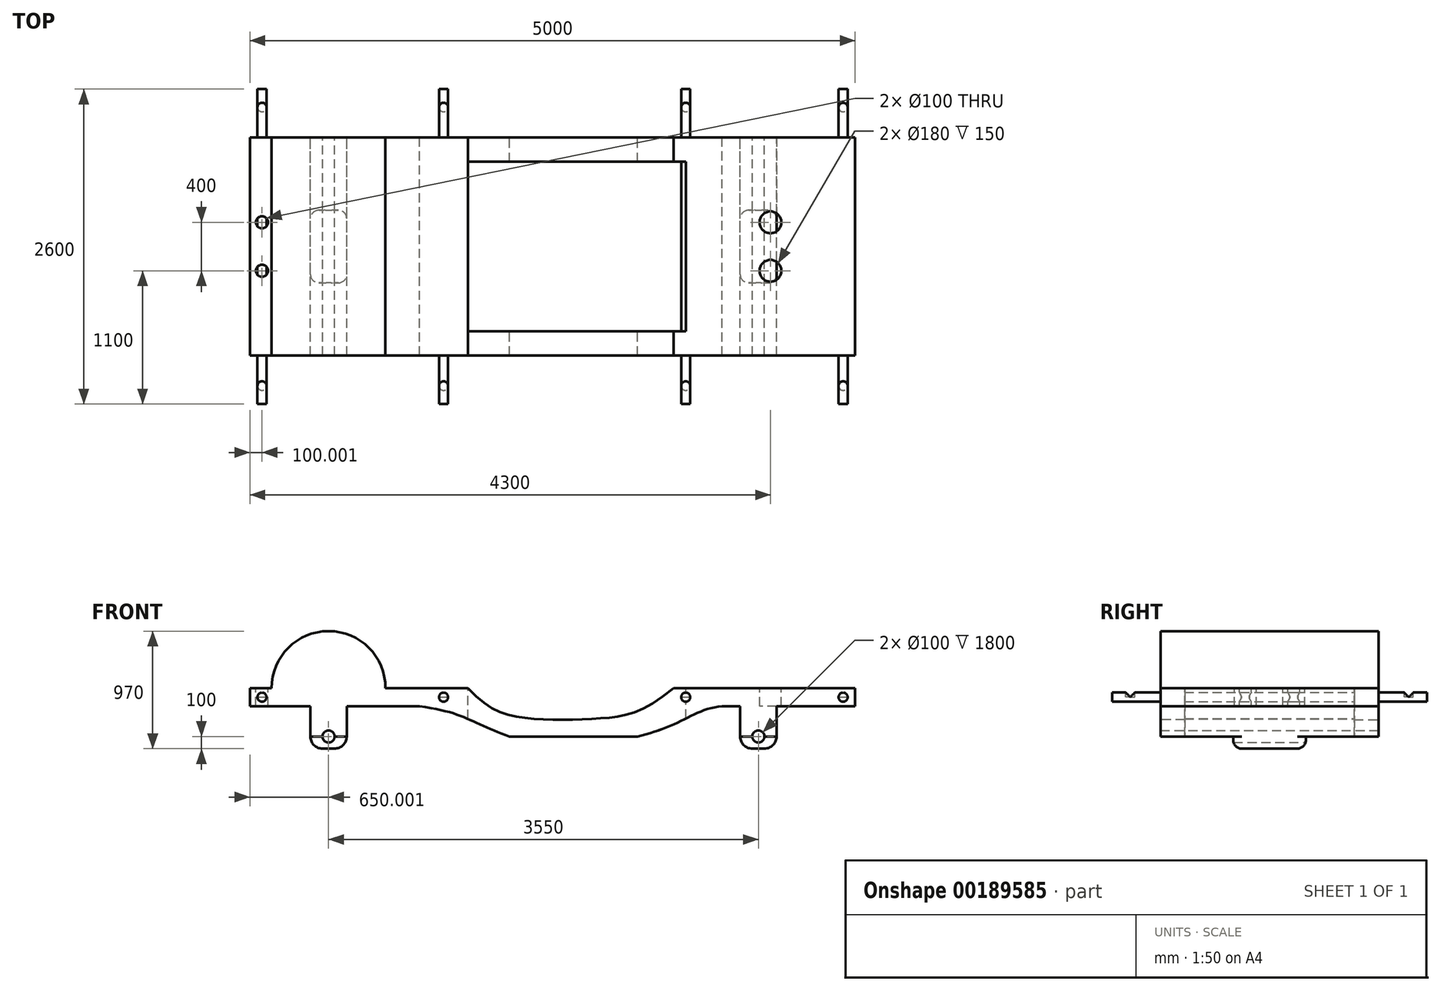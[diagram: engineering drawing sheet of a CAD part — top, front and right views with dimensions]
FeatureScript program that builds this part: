
annotation { "Feature Type Name" : "Feature", "Feature Type Description" : "" }
export const myFeature = defineFeature(function(context is Context, id is Id, definition is map)
    precondition{}
    {
        {
            var Q0;
            Q0=qCreatedBy(makeId("Front.planeOp"),FACE);
            var sketch = newSketch(context, id + "F0", { "sketchPlane" : qUnion([Q0])});
            skLineSegment(sketch, "E0", {"start": v(-2207.1, 0) * mm, "end": v(-2207.1, -150) * mm});
            skLineSegment(sketch, "E1", {"start": v(-2207.1, -150) * mm, "end": v(-807.1, -150) * mm});
            skFitSpline(sketch, "E2", {"points": [v(-807.1, -150) * mm, v(-307.1, -300) * mm, v(192.9, -450) * mm], "startDerivative": vector(1549.63, -206.62) * mm, "endDerivative": vector(1157.34, -66.43) * mm});
            skFitSpline(sketch, "E3", {"points": [v(192.9, -450) * mm, v(692.9, -450) * mm, v(1292.9, -300) * mm, v(1692.9, -150) * mm], "startDerivative": vector(931.79, -77.59) * mm, "endDerivative": vector(1482.21, 107.32) * mm});
            skLineSegment(sketch, "E4", {"start": v(1692.9, -150) * mm, "end": v(2792.9, -150) * mm});
            skLineSegment(sketch, "E5", {"start": v(2792.9, -150) * mm, "end": v(2792.9, 0) * mm});
            skLineSegment(sketch, "E6", {"start": v(-2207.1, 0) * mm, "end": v(-407.1, 0) * mm});
            skFitSpline(sketch, "E7", {"points": [v(-407.1, 0) * mm, v(92.9, -250) * mm, v(693, -250) * mm, v(1293, 0) * mm], "startDerivative": vector(1561.36, -1754.44) * mm, "endDerivative": vector(2212.71, 1856.89) * mm});
            skLineSegment(sketch, "E8", {"start": v(1293, 0) * mm, "end": v(2792.9, 0) * mm});
            skSolve(sketch);
        }
        {
            var Q0;
            Q0 = qSketchRegion(id + "F0", true);
            extrude(context, id + "F1", {"entities" : qUnion([Q0]), "depth" : 1800 * mm});
        }
        {
            var Q0;
            Q0=qCreatedBy(makeId("Top.planeOp"),FACE);
            var sketch = newSketch(context, id + "F2", { "sketchPlane" : qUnion([Q0])});
            skLineSegment(sketch, "E9.bottom", {"start": v(-407.1, -200) * mm, "end": v(1392.9, -200) * mm});
            skLineSegment(sketch, "E9.top", {"start": v(-407.1, -1600) * mm, "end": v(1392.9, -1600) * mm});
            skLineSegment(sketch, "E9.left", {"start": v(-407.1, -200) * mm, "end": v(-407.1, -1600) * mm});
            skLineSegment(sketch, "E9.right", {"start": v(1392.9, -200) * mm, "end": v(1392.9, -1600) * mm});
            skCircle(sketch, "E10", {"center": v(2092.9, -700) * mm, "radius": 90 * mm});
            skCircle(sketch, "E11", {"center": v(2092.9, -1100) * mm, "radius": 90 * mm});
            skCircle(sketch, "E12", {"center": v(-2107.1, -700) * mm, "radius": 50 * mm});
            skCircle(sketch, "E13", {"center": v(-2107.1, -1100) * mm, "radius": 50 * mm});
            skLineSegment(sketch, "E14", {"start": v(-2433.44, -900) * mm, "end": v(3216.39, -900) * mm, "construction": true});
            skSolve(sketch);
        }
        {
            var Q0;
            Q0=makeQuery(id+"F2.imprint","IMPRINT",FACE,{"disambiguationData":[TD([[makeQuery(id+"F2.imprint","IMPRINT",EDGE,{"derivedFrom":sQuery(id+"F2.wireOp",EDGE,"2RptNs6A-mePP-rphL-eACh-eVUUGwHWJbpe.bottom")}),-1.0]])]});
            var Q1;
            Q1=makeQuery(id+"F2.imprint","IMPRINT",FACE,{"disambiguationData":[TD([[makeQuery(id+"F2.imprint","IMPRINT",EDGE,{"derivedFrom":sQuery(id+"F2.wireOp",EDGE,"E9.bottom")}),-1.0]])]});
            var Q2;
            Q2=makeQuery(id+"F2.imprint","IMPRINT",FACE,{"disambiguationData":[TD([[makeQuery(id+"F2.imprint","IMPRINT",EDGE,{"derivedFrom":sQuery(id+"F2.wireOp",EDGE,"kMBfGQrs-vHd1-vmnO-5CYD-BuNOrFmh5Xz2.bottom")}),1.0]])]});
            var Q3;
            Q3=makeQuery(id+"F2.imprint","IMPRINT",FACE,{"disambiguationData":[TD([[makeQuery(id+"F2.imprint","IMPRINT",EDGE,{"derivedFrom":sQuery(id+"F2.wireOp",EDGE,"E11")}),1.0]])]});
            var Q4;
            Q4=makeQuery(id+"F2.imprint","IMPRINT",FACE,{"disambiguationData":[TD([[makeQuery(id+"F2.imprint","IMPRINT",EDGE,{"derivedFrom":sQuery(id+"F2.wireOp",EDGE,"E10")}),1.0]])]});
            var Q5;
            Q5=makeQuery(id+"F2.imprint","IMPRINT",FACE,{"disambiguationData":[TD([[makeQuery(id+"F2.imprint","IMPRINT",EDGE,{"derivedFrom":sQuery(id+"F2.wireOp",EDGE,"E12")}),1.0]])]});
            var Q6;
            Q6=makeQuery(id+"F2.imprint","IMPRINT",FACE,{"disambiguationData":[TD([[makeQuery(id+"F2.imprint","IMPRINT",EDGE,{"derivedFrom":sQuery(id+"F2.wireOp",EDGE,"E13")}),1.0]])]});
            extrude(context, id + "F3", {"entities" : qUnion([Q0, Q1, Q2, Q3, Q4, Q5, Q6]), "operationType" : NewBodyOperationType.REMOVE, "oppositeDirection" : true, "depth" : 1000 * mm, "hasSecondDirection" : true, "secondDirectionOppositeDirection" : false, "secondDirectionDepth" : 680 * mm});
        }
        {
            var Q0;
            Q0=makeQuery(id+"F2.imprint","IMPRINT",FACE,{"disambiguationData":[TD([[makeQuery(id+"F2.imprint","IMPRINT",EDGE,{"derivedFrom":sQuery(id+"F2.wireOp",EDGE,"E9.bottom")}),-1.0]])]});
            extrude(context, id + "F4", {"entities" : qUnion([Q0]), "operationType" : NewBodyOperationType.REMOVE, "depth" : 25 * mm});
        }
        {
            var Q0;
            Q0=qCreatedBy(makeId("Front.planeOp"),FACE);
            var sketch = newSketch(context, id + "F5", { "sketchPlane" : qUnion([Q0])});
            skLineSegment(sketch, "E15.bottom", {"start": v(1842.9, -150) * mm, "end": v(2142.9, -150) * mm});
            skLineSegment(sketch, "E15.top", {"start": v(1842.9, -500) * mm, "end": v(2142.9, -500) * mm});
            skLineSegment(sketch, "E15.left", {"start": v(1842.9, -150) * mm, "end": v(1842.9, -500) * mm});
            skLineSegment(sketch, "E15.right", {"start": v(2142.9, -150) * mm, "end": v(2142.9, -500) * mm});
            skLineSegment(sketch, "E16.bottom", {"start": v(-1707.1, -150) * mm, "end": v(-1407.1, -150) * mm});
            skLineSegment(sketch, "E16.top", {"start": v(-1707.1, -500) * mm, "end": v(-1407.1, -500) * mm});
            skLineSegment(sketch, "E16.left", {"start": v(-1707.1, -150) * mm, "end": v(-1707.1, -500) * mm});
            skLineSegment(sketch, "E16.right", {"start": v(-1407.1, -150) * mm, "end": v(-1407.1, -500) * mm});
            skCircle(sketch, "E17", {"center": v(-1557.1, -400) * mm, "radius": 50 * mm});
            skCircle(sketch, "E18", {"center": v(1992.9, -400) * mm, "radius": 50 * mm});
            skSolve(sketch);
        }
        {
            var Q0;
            Q0=makeQuery(id+"F5.imprint","IMPRINT",FACE,{"disambiguationData":[TD([[makeQuery(id+"F5.imprint","IMPRINT",EDGE,{"derivedFrom":sQuery(id+"F5.wireOp",EDGE,"E15.bottom")}),-1.0]])]});
            var Q1;
            Q1=makeQuery(id+"F5.imprint","IMPRINT",FACE,{"disambiguationData":[TD([[makeQuery(id+"F5.imprint","IMPRINT",EDGE,{"derivedFrom":sQuery(id+"F5.wireOp",EDGE,"E16.bottom")}),-1.0]])]});
            extrude(context, id + "F6", {"entities" : qUnion([Q0, Q1]), "operationType" : NewBodyOperationType.ADD, "depth" : 1800 * mm});
        }
        {
            var Q0;
            Q0=makeQuery(id+"F6.opExtrude","SWEPT_EDGE",EDGE,{"disambiguationData":[OSD([sQuery(id+"F5.wireOp",EDGE,"E16.top"),sQuery(id+"F5.wireOp",EDGE,"E16.left")])]});
            var Q1;
            Q1=makeQuery(id+"F6.opExtrude","SWEPT_EDGE",EDGE,{"disambiguationData":[OSD([sQuery(id+"F5.wireOp",EDGE,"E16.top"),sQuery(id+"F5.wireOp",EDGE,"E16.right")])]});
            var Q2;
            Q2=makeQuery(id+"F6.opExtrude","SWEPT_EDGE",EDGE,{"disambiguationData":[OSD([sQuery(id+"F5.wireOp",EDGE,"E15.top"),sQuery(id+"F5.wireOp",EDGE,"E15.left")])]});
            var Q3;
            Q3=makeQuery(id+"F6.opExtrude","SWEPT_EDGE",EDGE,{"disambiguationData":[OSD([sQuery(id+"F5.wireOp",EDGE,"E15.top"),sQuery(id+"F5.wireOp",EDGE,"E15.right")])]});
            fillet(context, id + "F7", {"entities" : qUnion([Q0, Q1, Q2, Q3]), "radius" : 100 * mm, "tangentPropagation" : true, "allowEdgeOverflow" : false});
        }
        {
            var Q0;
            Q0=makeQuery(id+"F6.opExtrude","SWEPT_FACE",FACE,{"disambiguationData":[OSD([sQuery(id+"F5.wireOp",EDGE,"E16.left")])]});
            var sketch = newSketch(context, id + "F8", { "sketchPlane" : qUnion([Q0])});
            skLineSegment(sketch, "E19.bottom", {"start": v(0, -550) * mm, "end": v(600, -550) * mm});
            skLineSegment(sketch, "E19.top", {"start": v(0, -400) * mm, "end": v(600, -400) * mm});
            skLineSegment(sketch, "E19.left", {"start": v(0, -550) * mm, "end": v(0, -400) * mm});
            skLineSegment(sketch, "E19.right", {"start": v(600, -550) * mm, "end": v(600, -400) * mm});
            skLineSegment(sketch, "E20.bottom", {"start": v(1200, -550) * mm, "end": v(1800, -550) * mm});
            skLineSegment(sketch, "E20.top", {"start": v(1200, -400) * mm, "end": v(1800, -400) * mm});
            skLineSegment(sketch, "E20.left", {"start": v(1200, -550) * mm, "end": v(1200, -400) * mm});
            skLineSegment(sketch, "E20.right", {"start": v(1800, -550) * mm, "end": v(1800, -400) * mm});
            skSolve(sketch);
        }
        {
            var Q0;
            {var subQ0=sQuery(id+"F8.wireOp",EDGE,"E20.bottom");Q0=makeQuery(id+"F8.imprint","IMPRINT",FACE,{"disambiguationData":[TD([[makeQuery(id+"F8.imprint","IMPRINT",EDGE,{"derivedFrom":subQ0}),1.0]])]});}
            var Q1;
            {var subQ0=sQuery(id+"F8.wireOp",EDGE,"E20.top");Q1=makeQuery(id+"F8.imprint","IMPRINT",FACE,{"disambiguationData":[TD([[makeQuery(id+"F8.imprint","IMPRINT",EDGE,{"derivedFrom":subQ0}),-1.0]])]});}
            var Q2;
            {var subQ0=sQuery(id+"F8.wireOp",EDGE,"E19.top");Q2=makeQuery(id+"F8.imprint","IMPRINT",FACE,{"disambiguationData":[TD([[makeQuery(id+"F8.imprint","IMPRINT",EDGE,{"derivedFrom":subQ0}),-1.0]])]});}
            var Q3;
            {var subQ0=sQuery(id+"F8.wireOp",EDGE,"E19.bottom");Q3=makeQuery(id+"F8.imprint","IMPRINT",FACE,{"disambiguationData":[TD([[makeQuery(id+"F8.imprint","IMPRINT",EDGE,{"derivedFrom":subQ0}),1.0]])]});}
            extrude(context, id + "F9", {"entities" : qUnion([Q0, Q1, Q2, Q3]), "operationType" : NewBodyOperationType.REMOVE, "oppositeDirection" : true, "depth" : 4000 * mm});
        }
        {
            var Q0;
            {var subQ0=sQuery(id+"F5.wireOp",EDGE,"E15.top");var subQ1=sQuery(id+"F8.wireOp",EDGE,"E19.right");Q0=makeQuery(id+"F9.boolean.opBoolean","COPY",EDGE,{"disambiguationData":[TD([makeQuery(id+"F6.opExtrude","SWEPT_FACE",FACE,{"disambiguationData":[OSD([subQ0])]})])],"derivedFrom":makeQuery(id+"F9.opExtrude","SWEPT_EDGE",EDGE,{"disambiguationData":[OSD([sQuery(id+"F8.wireOp",EDGE,"E19.bottom"),subQ1])]})});}
            var Q1;
            Q1=makeQuery(id+"F9.boolean.opBoolean","INTERSECT",EDGE,{"derivedFrom":[makeQuery(id+"F7.opFillet","BLEND_FACE",FACE,{"disambiguationData":[OSD([sQuery(id+"F5.wireOp",EDGE,"E15.top"),sQuery(id+"F5.wireOp",EDGE,"E15.right")])]}),makeQuery(id+"F9.opExtrude","SWEPT_FACE",FACE,{"disambiguationData":[OSD([sQuery(id+"F8.wireOp",EDGE,"E19.right")])]})]});
            var Q2;
            Q2=makeQuery(id+"F9.boolean.opBoolean","INTERSECT",EDGE,{"derivedFrom":[makeQuery(id+"F7.opFillet","BLEND_FACE",FACE,{"disambiguationData":[OSD([sQuery(id+"F5.wireOp",EDGE,"E15.top"),sQuery(id+"F5.wireOp",EDGE,"E15.right")])]}),makeQuery(id+"F9.opExtrude","SWEPT_FACE",FACE,{"disambiguationData":[OSD([sQuery(id+"F8.wireOp",EDGE,"E20.left")])]})]});
            var Q3;
            Q3=makeQuery(id+"F9.boolean.opBoolean","INTERSECT",EDGE,{"derivedFrom":[makeQuery(id+"F7.opFillet","BLEND_FACE",FACE,{"disambiguationData":[OSD([sQuery(id+"F5.wireOp",EDGE,"E16.top"),sQuery(id+"F5.wireOp",EDGE,"E16.left")])]}),makeQuery(id+"F9.opExtrude","SWEPT_FACE",FACE,{"disambiguationData":[OSD([sQuery(id+"F8.wireOp",EDGE,"E19.right")])]})]});
            var Q4;
            Q4=makeQuery(id+"F9.boolean.opBoolean","INTERSECT",EDGE,{"derivedFrom":[makeQuery(id+"F7.opFillet","BLEND_FACE",FACE,{"disambiguationData":[OSD([sQuery(id+"F5.wireOp",EDGE,"E16.top"),sQuery(id+"F5.wireOp",EDGE,"E16.left")])]}),makeQuery(id+"F9.opExtrude","SWEPT_FACE",FACE,{"disambiguationData":[OSD([sQuery(id+"F8.wireOp",EDGE,"E20.left")])]})]});
            fillet(context, id + "F10", {"entities" : qUnion([Q0, Q1, Q2, Q3, Q4]), "radius" : 70 * mm, "tangentPropagation" : true, "allowEdgeOverflow" : false});
        }
        {
            var Q0;
            Q0=makeQuery(id+"F6.boolean.opBoolean","MERGE",FACE,{"derivedFrom":[makeQuery(id+"F1.opExtrude","CAP_FACE",FACE,{"disambiguationData":[OSD([sQuery(id+"F0.wireOp",EDGE,"E0"),sQuery(id+"F0.wireOp",EDGE,"E1"),sQuery(id+"F0.wireOp",EDGE,"E2"),sQuery(id+"F0.wireOp",EDGE,"E3"),sQuery(id+"F0.wireOp",EDGE,"E4"),sQuery(id+"F0.wireOp",EDGE,"E5"),sQuery(id+"F0.wireOp",EDGE,"E6"),sQuery(id+"F0.wireOp",EDGE,"E7"),sQuery(id+"F0.wireOp",EDGE,"E8")])],"isStart":false}),makeQuery(id+"F6.opExtrude","CAP_FACE",FACE,{"disambiguationData":[OSD([sQuery(id+"F5.wireOp",EDGE,"E15.bottom"),sQuery(id+"F5.wireOp",EDGE,"E15.top"),sQuery(id+"F5.wireOp",EDGE,"E15.left"),sQuery(id+"F5.wireOp",EDGE,"E15.right"),sQuery(id+"F5.wireOp",EDGE,"E18")])],"isStart":false}),makeQuery(id+"F6.opExtrude","CAP_FACE",FACE,{"disambiguationData":[OSD([sQuery(id+"F5.wireOp",EDGE,"E16.bottom"),sQuery(id+"F5.wireOp",EDGE,"E16.top"),sQuery(id+"F5.wireOp",EDGE,"E16.left"),sQuery(id+"F5.wireOp",EDGE,"E16.right"),sQuery(id+"F5.wireOp",EDGE,"E17")])],"isStart":false})]});
            var sketch = newSketch(context, id + "F11", { "sketchPlane" : qUnion([Q0])});
            skArc(sketch, "E21", {"start": v(-1089.78, -50) * mm, "mid": v(-1557.1, 470) * mm, "end": v(-2024.44, -50) * mm});
            skLineSegment(sketch, "E22", {"start": v(-2024.44, -50) * mm, "end": v(-1089.78, -50) * mm});
            skSolve(sketch);
        }
        {
            var Q0;
            Q0=makeQuery(id+"F11.imprint","IMPRINT",FACE,{"disambiguationData":[TD([[makeQuery(id+"F11.imprint","IMPRINT",EDGE,{"derivedFrom":sQuery(id+"F11.wireOp",EDGE,"E21")}),1.0]])]});
            var Q1;
            {var subQ0=sQuery(id+"F11.wireOp",EDGE,"E21");var subQ1=makeQuery(id+"F1.opExtrude","CAP_EDGE",EDGE,{"disambiguationData":[OSD([sQuery(id+"F0.wireOp",EDGE,"E6")])],"isStart":false});var subQ2=makeQuery(id+"F11.imprint","INTERSECT",VERTEX,{"disambiguationData":[OD(0.0)],"derivedFrom":[subQ1,subQ0]});Q1=makeQuery(id+"F11.imprint","IMPRINT",FACE,{"disambiguationData":[TD([[makeQuery(id+"F11.imprint","IMPRINT",EDGE,{"disambiguationData":[TD([[subQ2,-1.0]])],"derivedFrom":subQ0}),1.0]])]});}
            extrude(context, id + "F12", {"entities" : qUnion([Q0, Q1]), "operationType" : NewBodyOperationType.ADD, "oppositeDirection" : true, "depth" : 1800 * mm});
        }
        {
            var Q0;
            Q0=makeQuery(id+"F12.boolean.opBoolean","MERGE",FACE,{"derivedFrom":[makeQuery(id+"F6.boolean.opBoolean","MERGE",FACE,{"derivedFrom":[makeQuery(id+"F1.opExtrude","CAP_FACE",FACE,{"disambiguationData":[OSD([sQuery(id+"F0.wireOp",EDGE,"E0"),sQuery(id+"F0.wireOp",EDGE,"E1"),sQuery(id+"F0.wireOp",EDGE,"E2"),sQuery(id+"F0.wireOp",EDGE,"E3"),sQuery(id+"F0.wireOp",EDGE,"E4"),sQuery(id+"F0.wireOp",EDGE,"E5"),sQuery(id+"F0.wireOp",EDGE,"E6"),sQuery(id+"F0.wireOp",EDGE,"E7"),sQuery(id+"F0.wireOp",EDGE,"E8")])],"isStart":false}),makeQuery(id+"F6.opExtrude","CAP_FACE",FACE,{"disambiguationData":[OSD([sQuery(id+"F5.wireOp",EDGE,"E15.bottom"),sQuery(id+"F5.wireOp",EDGE,"E15.top"),sQuery(id+"F5.wireOp",EDGE,"E15.left"),sQuery(id+"F5.wireOp",EDGE,"E15.right"),sQuery(id+"F5.wireOp",EDGE,"E18")])],"isStart":false}),makeQuery(id+"F6.opExtrude","CAP_FACE",FACE,{"disambiguationData":[OSD([sQuery(id+"F5.wireOp",EDGE,"E16.bottom"),sQuery(id+"F5.wireOp",EDGE,"E16.top"),sQuery(id+"F5.wireOp",EDGE,"E16.left"),sQuery(id+"F5.wireOp",EDGE,"E16.right"),sQuery(id+"F5.wireOp",EDGE,"E17")])],"isStart":false})]}),makeQuery(id+"F12.opExtrude","CAP_FACE",FACE,{"disambiguationData":[OSD([sQuery(id+"F11.wireOp",EDGE,"E21"),sQuery(id+"F11.wireOp",EDGE,"E22")])],"isStart":true})]});
            var sketch = newSketch(context, id + "F13", { "sketchPlane" : qUnion([Q0])});
            skCircle(sketch, "E23", {"center": v(-2107.1, -75) * mm, "radius": 37.5 * mm});
            skCircle(sketch, "E24", {"center": v(-607.1, -75) * mm, "radius": 37.5 * mm});
            skCircle(sketch, "E25", {"center": v(2692.9, -75) * mm, "radius": 37.5 * mm});
            skCircle(sketch, "E26", {"center": v(1392.9, -75) * mm, "radius": 37.5 * mm});
            skSolve(sketch);
        }
        {
            var Q0;
            Q0=makeQuery(id+"F13.imprint","IMPRINT",FACE,{"disambiguationData":[TD([[makeQuery(id+"F13.imprint","IMPRINT",EDGE,{"derivedFrom":sQuery(id+"F13.wireOp",EDGE,"E23")}),1.0]])]});
            var Q1;
            Q1=makeQuery(id+"F13.imprint","IMPRINT",FACE,{"disambiguationData":[TD([[makeQuery(id+"F13.imprint","IMPRINT",EDGE,{"derivedFrom":sQuery(id+"F13.wireOp",EDGE,"E24")}),1.0]])]});
            var Q2;
            Q2=makeQuery(id+"F13.imprint","IMPRINT",FACE,{"disambiguationData":[TD([[makeQuery(id+"F13.imprint","IMPRINT",EDGE,{"derivedFrom":sQuery(id+"F13.wireOp",EDGE,"E26")}),1.0]])]});
            var Q3;
            Q3=makeQuery(id+"F13.imprint","IMPRINT",FACE,{"disambiguationData":[TD([[makeQuery(id+"F13.imprint","IMPRINT",EDGE,{"derivedFrom":sQuery(id+"F13.wireOp",EDGE,"E25")}),1.0]])]});
            extrude(context, id + "F14", {"entities" : qUnion([Q0, Q1, Q2, Q3]), "operationType" : NewBodyOperationType.ADD, "depth" : 400 * mm, "hasSecondDirection" : true, "secondDirectionOppositeDirection" : true, "secondDirectionDepth" : 2200 * mm});
        }
        {
            var Q0;
            Q0=qCreatedBy(makeId("Top.planeOp"),FACE);
            var sketch = newSketch(context, id + "F15", { "sketchPlane" : qUnion([Q0])});
            skCircle(sketch, "E27", {"center": v(-2107.1, -2050) * mm, "radius": 37.5 * mm});
            skCircle(sketch, "E28", {"center": v(-2107.1, 250) * mm, "radius": 37.5 * mm});
            skLineSegment(sketch, "E29", {"start": v(-2107.1, -2429.92) * mm, "end": v(-2107.1, 1499.1) * mm, "construction": true});
            skLineSegment(sketch, "E30", {"start": v(-607.1, -2303.55) * mm, "end": v(-607.1, 1372.73) * mm, "construction": true});
            skCircle(sketch, "E31", {"center": v(-607.1, -2050) * mm, "radius": 37.5 * mm});
            skCircle(sketch, "E32", {"center": v(-607.1, 250) * mm, "radius": 37.5 * mm});
            skLineSegment(sketch, "E33", {"start": v(1392.9, 663.92) * mm, "end": v(1392.9, -2150.45) * mm, "construction": true});
            skLineSegment(sketch, "E34", {"start": v(2692.9, -2329.14) * mm, "end": v(2692.9, 858.87) * mm, "construction": true});
            skCircle(sketch, "E35", {"center": v(1392.9, 250) * mm, "radius": 37.5 * mm});
            skCircle(sketch, "E36", {"center": v(2692.9, 250) * mm, "radius": 37.5 * mm});
            skCircle(sketch, "E37", {"center": v(1392.9, -2050) * mm, "radius": 37.5 * mm});
            skCircle(sketch, "E38", {"center": v(2692.9, -2050) * mm, "radius": 37.5 * mm});
            skSolve(sketch);
        }
        {
            var Q0;
            Q0=makeQuery(id+"F15.imprint","IMPRINT",FACE,{"disambiguationData":[TD([[makeQuery(id+"F15.imprint","IMPRINT",EDGE,{"derivedFrom":sQuery(id+"F15.wireOp",EDGE,"E27")}),1.0]])]});
            var Q1;
            Q1=makeQuery(id+"F15.imprint","IMPRINT",FACE,{"disambiguationData":[TD([[makeQuery(id+"F15.imprint","IMPRINT",EDGE,{"derivedFrom":sQuery(id+"F15.wireOp",EDGE,"E28")}),1.0]])]});
            var Q2;
            Q2=makeQuery(id+"F15.imprint","IMPRINT",FACE,{"disambiguationData":[TD([[makeQuery(id+"F15.imprint","IMPRINT",EDGE,{"derivedFrom":sQuery(id+"F15.wireOp",EDGE,"E31")}),1.0]])]});
            var Q3;
            Q3=makeQuery(id+"F15.imprint","IMPRINT",FACE,{"disambiguationData":[TD([[makeQuery(id+"F15.imprint","IMPRINT",EDGE,{"derivedFrom":sQuery(id+"F15.wireOp",EDGE,"E32")}),1.0]])]});
            var Q4;
            Q4=makeQuery(id+"F15.imprint","IMPRINT",FACE,{"disambiguationData":[TD([[makeQuery(id+"F15.imprint","IMPRINT",EDGE,{"derivedFrom":sQuery(id+"F15.wireOp",EDGE,"E36")}),1.0]])]});
            var Q5;
            Q5=makeQuery(id+"F15.imprint","IMPRINT",FACE,{"disambiguationData":[TD([[makeQuery(id+"F15.imprint","IMPRINT",EDGE,{"derivedFrom":sQuery(id+"F15.wireOp",EDGE,"E37")}),1.0]])]});
            var Q6;
            Q6=makeQuery(id+"F15.imprint","IMPRINT",FACE,{"disambiguationData":[TD([[makeQuery(id+"F15.imprint","IMPRINT",EDGE,{"derivedFrom":sQuery(id+"F15.wireOp",EDGE,"E38")}),1.0]])]});
            var Q7;
            Q7=makeQuery(id+"F15.imprint","IMPRINT",FACE,{"disambiguationData":[TD([[makeQuery(id+"F15.imprint","IMPRINT",EDGE,{"derivedFrom":sQuery(id+"F15.wireOp",EDGE,"E35")}),1.0]])]});
            extrude(context, id + "F16", {"entities" : qUnion([Q0, Q1, Q2, Q3, Q4, Q5, Q6, Q7]), "operationType" : NewBodyOperationType.REMOVE, "oppositeDirection" : true, "depth" : 75 * mm});
        }
    });
